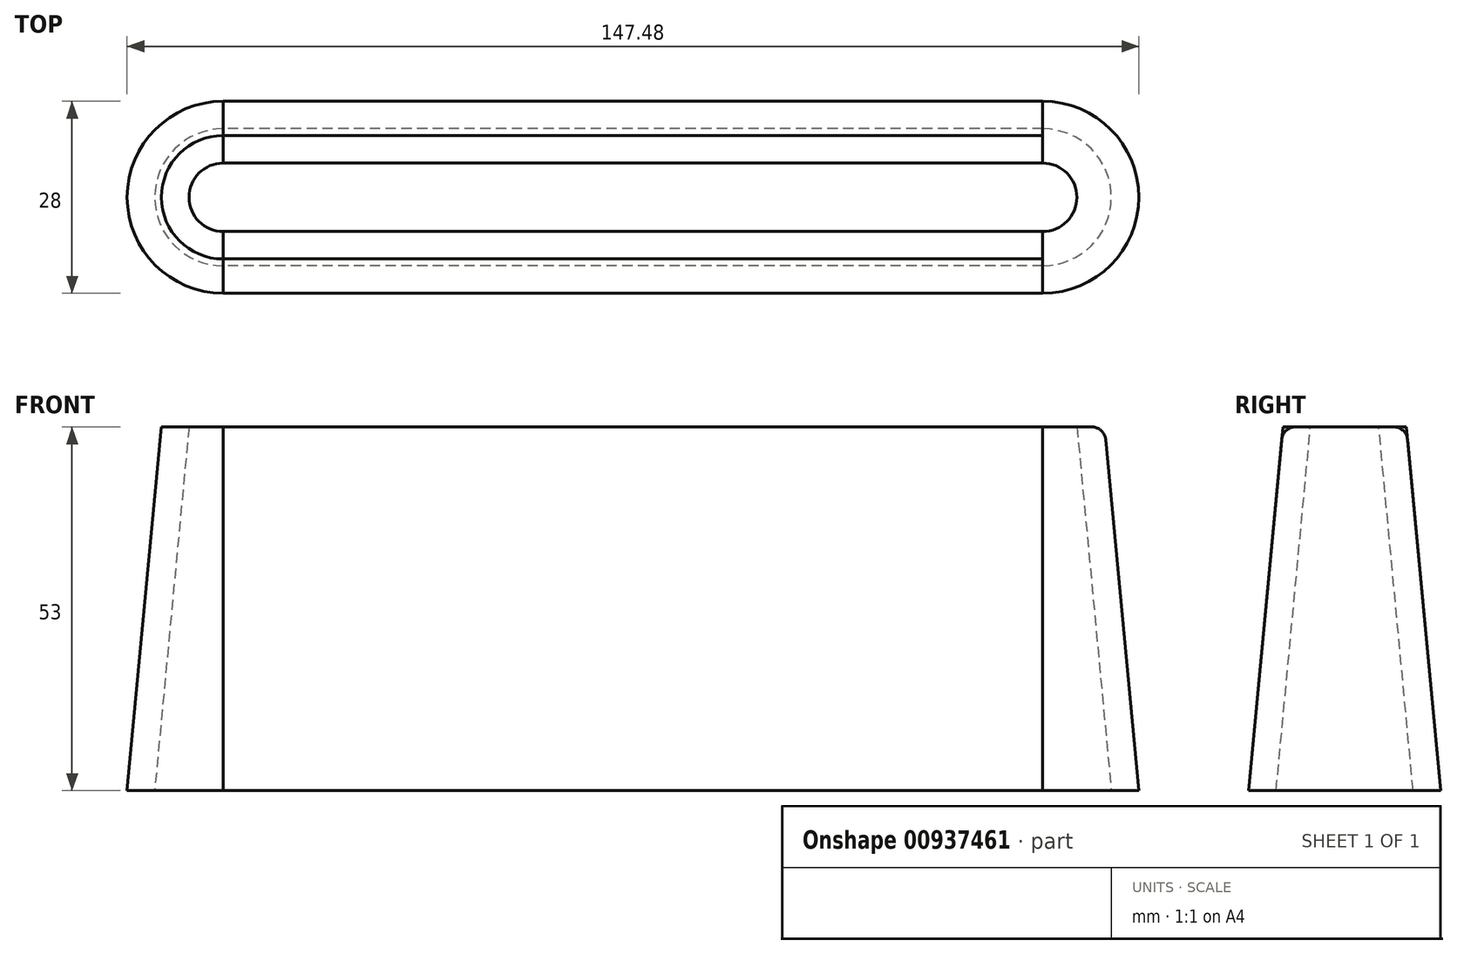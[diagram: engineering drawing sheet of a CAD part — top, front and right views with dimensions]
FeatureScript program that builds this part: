
annotation { "Feature Type Name" : "Feature", "Feature Type Description" : "" }
export const myFeature = defineFeature(function(context is Context, id is Id, definition is map)
    precondition{}
    {
        {
            var Q0;
            Q0=qCreatedBy(makeId("Front.planeOp"),FACE);
            var sketch = newSketch(context, id + "F0", { "sketchPlane" : qUnion([Q0])});
            skLineSegment(sketch, "E0.bottom", {"start": v(76.26, -26.5) * mm, "end": v(-73.74, -26.5) * mm});
            skLineSegment(sketch, "E0.top", {"start": v(76.26, 26.5) * mm, "end": v(-73.74, 26.5) * mm});
            skLineSegment(sketch, "E0.left", {"start": v(76.26, -26.5) * mm, "end": v(76.26, 26.5) * mm});
            skLineSegment(sketch, "E0.right", {"start": v(-73.74, -26.5) * mm, "end": v(-73.74, 26.5) * mm});
            skPoint(sketch, "E0.middle", {"position": v(1.26, 0) * mm});
            skLineSegment(sketch, "E1", {"start": v(-73.74, -26.5) * mm, "end": v(-68.74, 26.5) * mm});
            skLineSegment(sketch, "E2", {"start": v(-69.72, -26.5) * mm, "end": v(-64.72, 26.5) * mm});
            skLineSegment(sketch, "E3", {"start": v(-59.74, 26.5) * mm, "end": v(-59.74, -26.5) * mm});
            skSolve(sketch);
        }
        {
            var Q0;
            {var subQ0=sQuery(id+"F0.wireOp",EDGE,"E1");Q0=makeQuery(id+"F0.imprint","IMPRINT",FACE,{"disambiguationData":[TD([[makeQuery(id+"F0.imprint","IMPRINT",EDGE,{"derivedFrom":subQ0}),-1.0]])]});}
            var Q1;
            Q1=sQuery(id+"F0.wireOp",EDGE,"E3");
            revolve(context, id + "F1", {"surfaceOperationType" : NewSurfaceOperationType.NEW, "entities" : qUnion([Q0]), "axis" : qUnion([Q1]), "revolveType" : RevolveType.SYMMETRIC, "angle" : 180 * degree});
        }
        {
            var Q0;
            Q0=makeQuery(id+"F1.opRevolve","SWEPT_BODY",BODY,{"disambiguationData":[OSD([sQuery(id+"F0.wireOp",EDGE,"E0.bottom"),sQuery(id+"F0.wireOp",EDGE,"E0.top"),sQuery(id+"F0.wireOp",EDGE,"E1"),sQuery(id+"F0.wireOp",EDGE,"E2")])]});
            var Q1;
            Q1=qCreatedBy(makeId("Right.planeOp"),FACE);
            mirror(context, id + "F2", {"entities" : qUnion([Q0]), "mirrorPlane" : qUnion([Q1])});
        }
        {
            var Q0;
            Q0=makeQuery(id+"F1.opRevolve","CAP_FACE",FACE,{"disambiguationData":[OSD([sQuery(id+"F0.wireOp",EDGE,"E0.bottom"),sQuery(id+"F0.wireOp",EDGE,"E0.top"),sQuery(id+"F0.wireOp",EDGE,"E1"),sQuery(id+"F0.wireOp",EDGE,"E2")])],"isStart":true});
            var Q1;
            Q1=makeQuery(id+"F1.opRevolve","CAP_FACE",FACE,{"disambiguationData":[OSD([sQuery(id+"F0.wireOp",EDGE,"E0.bottom"),sQuery(id+"F0.wireOp",EDGE,"E0.top"),sQuery(id+"F0.wireOp",EDGE,"E1"),sQuery(id+"F0.wireOp",EDGE,"E2")])],"isStart":false});
            extrude(context, id + "F3", {"entities" : qUnion([Q0, Q1]), "endBound" : BoundingType.UP_TO_NEXT, "depth" : 25 * mm, "offsetDistance" : 25 * mm});
        }
        {
            var Q0;
            Q0=makeQuery(id+"F2.opPattern","COPY",EDGE,{"derivedFrom":makeQuery(id+"F1.opRevolve","SWEPT_EDGE",EDGE,{"disambiguationData":[OSD([sQuery(id+"F0.wireOp",EDGE,"E0.top"),sQuery(id+"F0.wireOp",EDGE,"E1")])]}),"instanceName":"1"});
            fillet(context, id + "F4", {"entities" : qUnion([Q0]), "radius" : 2 * mm, "tangentPropagation" : true, "allowEdgeOverflow" : false});
        }
    });
